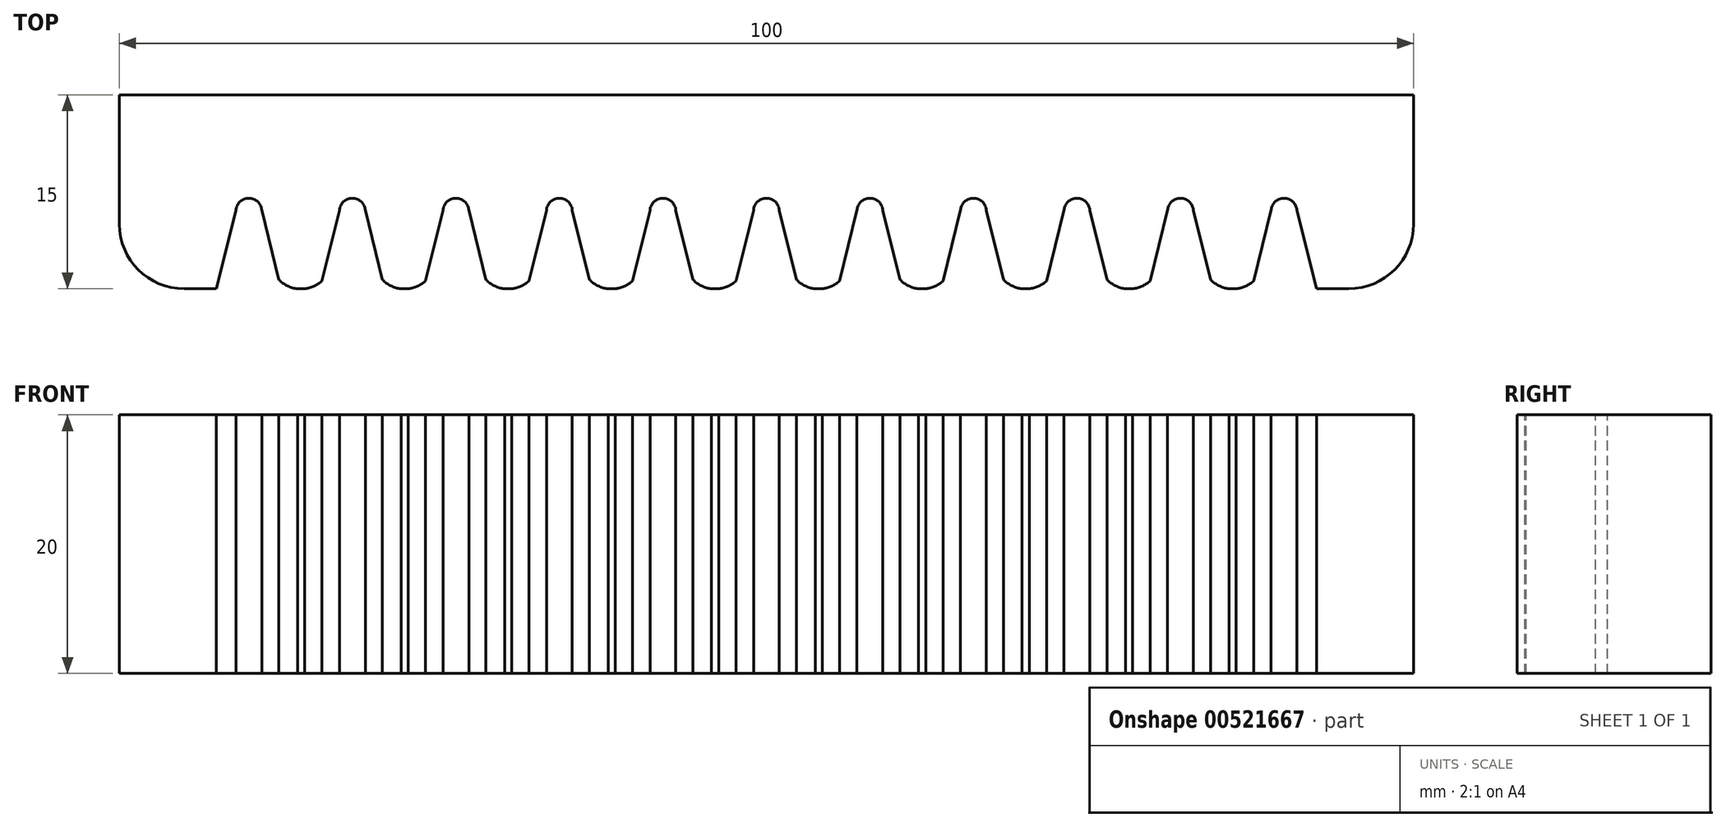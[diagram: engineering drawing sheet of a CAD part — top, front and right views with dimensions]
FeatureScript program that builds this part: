
annotation { "Feature Type Name" : "Feature", "Feature Type Description" : "" }
export const myFeature = defineFeature(function(context is Context, id is Id, definition is map)
    precondition{}
    {
        {
            var Q0;
            Q0=qCreatedBy(makeId("Front.planeOp"),FACE);
            var sketch = newSketch(context, id + "F0", { "sketchPlane" : qUnion([Q0])});
            skLineSegment(sketch, "E0.bottom", {"start": v(50, -10) * mm, "end": v(-50, -10) * mm});
            skLineSegment(sketch, "E0.top", {"start": v(50, 10) * mm, "end": v(-50, 10) * mm});
            skLineSegment(sketch, "E0.left", {"start": v(50, -10) * mm, "end": v(50, 10) * mm});
            skLineSegment(sketch, "E0.right", {"start": v(-50, -10) * mm, "end": v(-50, 10) * mm});
            skPoint(sketch, "E0.middle", {"position": v(0, 0) * mm});
            skSolve(sketch);
        }
        {
            var Q0;
            Q0 = qSketchRegion(id + "F0", true);
            extrude(context, id + "F1", {"entities" : qUnion([Q0]), "depth" : 15 * mm, "offsetDistance" : 25 * mm});
        }
        {
            var Q0;
            Q0=makeQuery(id+"F1.opExtrude","SWEPT_FACE",FACE,{"disambiguationData":[OSD([sQuery(id+"F0.wireOp",EDGE,"E0.top")])]});
            var sketch = newSketch(context, id + "F2", { "sketchPlane" : qUnion([Q0])});
            skLineSegment(sketch, "E1", {"start": v(0, 0) * mm, "end": v(0, -15) * mm, "construction": true});
            skArc(sketch, "E2", {"start": v(1, -8.94) * mm, "mid": v(0, -8) * mm, "end": v(-1, -8.94) * mm});
            skLineSegment(sketch, "E3", {"start": v(-1, -8.94) * mm, "end": v(-2.5, -15) * mm});
            skLineSegment(sketch, "E4.MirrorCS", {"start": v(1, -8.94) * mm, "end": v(2.5, -15) * mm});
            skPoint(sketch, "E5.center.orphan", {"position": v(0, -12.5) * mm});
            skPoint(sketch, "E6.center.orphan", {"position": v(0, -10.5) * mm});
            skLineSegment(sketch, "E7.1.0.0", {"start": v(9, -8.94) * mm, "end": v(10.5, -15) * mm});
            skArc(sketch, "E7.1.0.1", {"start": v(9, -8.94) * mm, "mid": v(8, -8) * mm, "end": v(7, -8.94) * mm});
            skLineSegment(sketch, "E7.1.0.2", {"start": v(7, -8.94) * mm, "end": v(5.5, -15) * mm});
            skLineSegment(sketch, "E7.2.0.0", {"start": v(17, -8.94) * mm, "end": v(18.5, -15) * mm});
            skArc(sketch, "E7.2.0.1", {"start": v(17, -8.94) * mm, "mid": v(16, -8) * mm, "end": v(15, -8.94) * mm});
            skLineSegment(sketch, "E7.2.0.2", {"start": v(15, -8.94) * mm, "end": v(13.5, -15) * mm});
            skLineSegment(sketch, "E7.3.0.0", {"start": v(25, -8.94) * mm, "end": v(26.5, -15) * mm});
            skArc(sketch, "E7.3.0.1", {"start": v(25, -8.94) * mm, "mid": v(24, -8) * mm, "end": v(23, -8.94) * mm});
            skLineSegment(sketch, "E7.3.0.2", {"start": v(23, -8.94) * mm, "end": v(21.5, -15) * mm});
            skLineSegment(sketch, "E7.4.0.0", {"start": v(33, -8.94) * mm, "end": v(34.5, -15) * mm});
            skArc(sketch, "E7.4.0.1", {"start": v(33, -8.94) * mm, "mid": v(32, -8) * mm, "end": v(31, -8.94) * mm});
            skLineSegment(sketch, "E7.4.0.2", {"start": v(31, -8.94) * mm, "end": v(29.5, -15) * mm});
            skLineSegment(sketch, "E7.5.0.0", {"start": v(41, -8.94) * mm, "end": v(42.5, -15) * mm});
            skArc(sketch, "E7.5.0.1", {"start": v(41, -8.94) * mm, "mid": v(40, -8) * mm, "end": v(39, -8.94) * mm});
            skLineSegment(sketch, "E7.5.0.2", {"start": v(39, -8.94) * mm, "end": v(37.5, -15) * mm});
            skLineSegment(sketch, "E7.direction1", {"start": v(2.5, -15) * mm, "end": v(10.5, -15) * mm, "construction": true});
            skLineSegment(sketch, "E8.1.0.0", {"start": v(-9, -8.94) * mm, "end": v(-10.5, -15) * mm});
            skArc(sketch, "E8.1.0.1", {"start": v(-7, -8.94) * mm, "mid": v(-8, -8) * mm, "end": v(-9, -8.94) * mm});
            skLineSegment(sketch, "E8.1.0.2", {"start": v(-7, -8.94) * mm, "end": v(-5.5, -15) * mm});
            skLineSegment(sketch, "E8.2.0.0", {"start": v(-17, -8.94) * mm, "end": v(-18.5, -15) * mm});
            skArc(sketch, "E8.2.0.1", {"start": v(-15, -8.94) * mm, "mid": v(-16, -8) * mm, "end": v(-17, -8.94) * mm});
            skLineSegment(sketch, "E8.2.0.2", {"start": v(-15, -8.94) * mm, "end": v(-13.5, -15) * mm});
            skLineSegment(sketch, "E8.3.0.0", {"start": v(-25, -8.94) * mm, "end": v(-26.5, -15) * mm});
            skArc(sketch, "E8.3.0.1", {"start": v(-23, -8.94) * mm, "mid": v(-24, -8) * mm, "end": v(-25, -8.94) * mm});
            skLineSegment(sketch, "E8.3.0.2", {"start": v(-23, -8.94) * mm, "end": v(-21.5, -15) * mm});
            skLineSegment(sketch, "E8.4.0.0", {"start": v(-33, -8.94) * mm, "end": v(-34.5, -15) * mm});
            skArc(sketch, "E8.4.0.1", {"start": v(-31, -8.94) * mm, "mid": v(-32, -8) * mm, "end": v(-33, -8.94) * mm});
            skLineSegment(sketch, "E8.4.0.2", {"start": v(-31, -8.94) * mm, "end": v(-29.5, -15) * mm});
            skLineSegment(sketch, "E8.5.0.0", {"start": v(-41, -8.94) * mm, "end": v(-42.5, -15) * mm});
            skArc(sketch, "E8.5.0.1", {"start": v(-39, -8.94) * mm, "mid": v(-40, -8) * mm, "end": v(-41, -8.94) * mm});
            skLineSegment(sketch, "E8.5.0.2", {"start": v(-39, -8.94) * mm, "end": v(-37.5, -15) * mm});
            skLineSegment(sketch, "E8.direction1", {"start": v(-2.5, -15) * mm, "end": v(-10.5, -15) * mm, "construction": true});
            skArc(sketch, "E9", {"start": v(2.33, -14.3) * mm, "mid": v(3.97, -15.01) * mm, "end": v(5.65, -14.39) * mm});
            skArc(sketch, "E10.1.0.0", {"start": v(10.33, -14.3) * mm, "mid": v(11.97, -15.01) * mm, "end": v(13.65, -14.39) * mm});
            skArc(sketch, "E10.2.0.0", {"start": v(18.33, -14.3) * mm, "mid": v(19.97, -15.01) * mm, "end": v(21.65, -14.39) * mm});
            skArc(sketch, "E10.3.0.0", {"start": v(26.33, -14.3) * mm, "mid": v(27.97, -15.01) * mm, "end": v(29.65, -14.39) * mm});
            skArc(sketch, "E10.4.0.0", {"start": v(34.33, -14.3) * mm, "mid": v(35.97, -15.01) * mm, "end": v(37.65, -14.39) * mm});
            skLineSegment(sketch, "E10.direction1", {"start": v(2.33, -14.3) * mm, "end": v(10.33, -14.3) * mm, "construction": true});
            skArc(sketch, "E11.1.0.0", {"start": v(-5.67, -14.3) * mm, "mid": v(-4.03, -15.01) * mm, "end": v(-2.35, -14.39) * mm});
            skArc(sketch, "E11.2.0.0", {"start": v(-13.67, -14.3) * mm, "mid": v(-12.03, -15.01) * mm, "end": v(-10.35, -14.39) * mm});
            skArc(sketch, "E11.3.0.0", {"start": v(-21.67, -14.3) * mm, "mid": v(-20.03, -15.01) * mm, "end": v(-18.35, -14.39) * mm});
            skArc(sketch, "E11.4.0.0", {"start": v(-29.67, -14.3) * mm, "mid": v(-28.03, -15.01) * mm, "end": v(-26.35, -14.39) * mm});
            skArc(sketch, "E11.5.0.0", {"start": v(-37.67, -14.3) * mm, "mid": v(-36.03, -15.01) * mm, "end": v(-34.35, -14.39) * mm});
            skLineSegment(sketch, "E11.direction1", {"start": v(2.33, -14.3) * mm, "end": v(-5.67, -14.3) * mm, "construction": true});
            skSolve(sketch);
        }
        {
            var Q0;
            {var subQ0=sQuery(id+"F2.wireOp",EDGE,"E8.5.0.0");Q0=makeQuery(id+"F2.imprint","IMPRINT",FACE,{"disambiguationData":[TD([[makeQuery(id+"F2.imprint","IMPRINT",EDGE,{"derivedFrom":subQ0}),1.0]])]});}
            var Q1;
            {var subQ0=sQuery(id+"F2.wireOp",EDGE,"E8.4.0.0");Q1=makeQuery(id+"F2.imprint","IMPRINT",FACE,{"disambiguationData":[TD([[makeQuery(id+"F2.imprint","IMPRINT",EDGE,{"derivedFrom":subQ0}),1.0]])]});}
            var Q2;
            {var subQ0=sQuery(id+"F2.wireOp",EDGE,"E8.3.0.0");Q2=makeQuery(id+"F2.imprint","IMPRINT",FACE,{"disambiguationData":[TD([[makeQuery(id+"F2.imprint","IMPRINT",EDGE,{"derivedFrom":subQ0}),1.0]])]});}
            var Q3;
            {var subQ0=sQuery(id+"F2.wireOp",EDGE,"E8.2.0.0");Q3=makeQuery(id+"F2.imprint","IMPRINT",FACE,{"disambiguationData":[TD([[makeQuery(id+"F2.imprint","IMPRINT",EDGE,{"derivedFrom":subQ0}),1.0]])]});}
            var Q4;
            {var subQ0=sQuery(id+"F2.wireOp",EDGE,"E8.1.0.0");Q4=makeQuery(id+"F2.imprint","IMPRINT",FACE,{"disambiguationData":[TD([[makeQuery(id+"F2.imprint","IMPRINT",EDGE,{"derivedFrom":subQ0}),1.0]])]});}
            var Q5;
            Q5=makeQuery(id+"F2.imprint","IMPRINT",FACE,{"disambiguationData":[TD([[makeQuery(id+"F2.imprint","IMPRINT",EDGE,{"derivedFrom":sQuery(id+"F2.wireOp",EDGE,"E2")}),1.0]])]});
            var Q6;
            {var subQ0=sQuery(id+"F2.wireOp",EDGE,"E7.1.0.0");Q6=makeQuery(id+"F2.imprint","IMPRINT",FACE,{"disambiguationData":[TD([[makeQuery(id+"F2.imprint","IMPRINT",EDGE,{"derivedFrom":subQ0}),-1.0]])]});}
            var Q7;
            {var subQ0=sQuery(id+"F2.wireOp",EDGE,"E7.2.0.0");Q7=makeQuery(id+"F2.imprint","IMPRINT",FACE,{"disambiguationData":[TD([[makeQuery(id+"F2.imprint","IMPRINT",EDGE,{"derivedFrom":subQ0}),-1.0]])]});}
            var Q8;
            {var subQ0=sQuery(id+"F2.wireOp",EDGE,"E7.3.0.0");Q8=makeQuery(id+"F2.imprint","IMPRINT",FACE,{"disambiguationData":[TD([[makeQuery(id+"F2.imprint","IMPRINT",EDGE,{"derivedFrom":subQ0}),-1.0]])]});}
            var Q9;
            {var subQ0=sQuery(id+"F2.wireOp",EDGE,"E7.4.0.0");Q9=makeQuery(id+"F2.imprint","IMPRINT",FACE,{"disambiguationData":[TD([[makeQuery(id+"F2.imprint","IMPRINT",EDGE,{"derivedFrom":subQ0}),-1.0]])]});}
            var Q10;
            {var subQ0=sQuery(id+"F2.wireOp",EDGE,"E7.5.0.0");Q10=makeQuery(id+"F2.imprint","IMPRINT",FACE,{"disambiguationData":[TD([[makeQuery(id+"F2.imprint","IMPRINT",EDGE,{"derivedFrom":subQ0}),-1.0]])]});}
            var Q11;
            {var subQ0=sQuery(id+"F2.wireOp",EDGE,"E7.2.0.2");var subQ1=makeQuery(id+"F1.opExtrude","CAP_EDGE",EDGE,{"disambiguationData":[OSD([sQuery(id+"F0.wireOp",EDGE,"E0.top")])],"isStart":false});var subQ2=makeQuery(id+"F2.imprint","INTERSECT",VERTEX,{"derivedFrom":[subQ1,subQ0]});Q11=makeQuery(id+"F2.imprint","IMPRINT",FACE,{"disambiguationData":[TD([[makeQuery(id+"F2.imprint","IMPRINT",EDGE,{"disambiguationData":[TD([[subQ2,1.0]])],"derivedFrom":subQ0}),-1.0]])]});}
            var Q12;
            {var subQ0=sQuery(id+"F2.wireOp",EDGE,"E7.1.0.0");var subQ1=makeQuery(id+"F1.opExtrude","CAP_EDGE",EDGE,{"disambiguationData":[OSD([sQuery(id+"F0.wireOp",EDGE,"E0.top")])],"isStart":false});var subQ2=makeQuery(id+"F2.imprint","INTERSECT",VERTEX,{"derivedFrom":[subQ1,subQ0]});Q12=makeQuery(id+"F2.imprint","IMPRINT",FACE,{"disambiguationData":[TD([[makeQuery(id+"F2.imprint","IMPRINT",EDGE,{"disambiguationData":[TD([[subQ2,1.0]])],"derivedFrom":subQ0}),1.0]])]});}
            var Q13;
            {var subQ0=sQuery(id+"F2.wireOp",EDGE,"E7.2.0.0");var subQ1=makeQuery(id+"F1.opExtrude","CAP_EDGE",EDGE,{"disambiguationData":[OSD([sQuery(id+"F0.wireOp",EDGE,"E0.top")])],"isStart":false});var subQ2=makeQuery(id+"F2.imprint","INTERSECT",VERTEX,{"derivedFrom":[subQ1,subQ0]});Q13=makeQuery(id+"F2.imprint","IMPRINT",FACE,{"disambiguationData":[TD([[makeQuery(id+"F2.imprint","IMPRINT",EDGE,{"disambiguationData":[TD([[subQ2,1.0]])],"derivedFrom":subQ0}),1.0]])]});}
            var Q14;
            {var subQ0=sQuery(id+"F2.wireOp",EDGE,"E7.3.0.2");var subQ1=makeQuery(id+"F1.opExtrude","CAP_EDGE",EDGE,{"disambiguationData":[OSD([sQuery(id+"F0.wireOp",EDGE,"E0.top")])],"isStart":false});var subQ2=makeQuery(id+"F2.imprint","INTERSECT",VERTEX,{"derivedFrom":[subQ1,subQ0]});Q14=makeQuery(id+"F2.imprint","IMPRINT",FACE,{"disambiguationData":[TD([[makeQuery(id+"F2.imprint","IMPRINT",EDGE,{"disambiguationData":[TD([[subQ2,1.0]])],"derivedFrom":subQ0}),-1.0]])]});}
            var Q15;
            {var subQ0=sQuery(id+"F2.wireOp",EDGE,"E7.3.0.0");var subQ1=makeQuery(id+"F1.opExtrude","CAP_EDGE",EDGE,{"disambiguationData":[OSD([sQuery(id+"F0.wireOp",EDGE,"E0.top")])],"isStart":false});var subQ2=makeQuery(id+"F2.imprint","INTERSECT",VERTEX,{"derivedFrom":[subQ1,subQ0]});Q15=makeQuery(id+"F2.imprint","IMPRINT",FACE,{"disambiguationData":[TD([[makeQuery(id+"F2.imprint","IMPRINT",EDGE,{"disambiguationData":[TD([[subQ2,1.0]])],"derivedFrom":subQ0}),1.0]])]});}
            var Q16;
            {var subQ0=sQuery(id+"F2.wireOp",EDGE,"E7.4.0.2");var subQ1=makeQuery(id+"F1.opExtrude","CAP_EDGE",EDGE,{"disambiguationData":[OSD([sQuery(id+"F0.wireOp",EDGE,"E0.top")])],"isStart":false});var subQ2=makeQuery(id+"F2.imprint","INTERSECT",VERTEX,{"derivedFrom":[subQ1,subQ0]});Q16=makeQuery(id+"F2.imprint","IMPRINT",FACE,{"disambiguationData":[TD([[makeQuery(id+"F2.imprint","IMPRINT",EDGE,{"disambiguationData":[TD([[subQ2,1.0]])],"derivedFrom":subQ0}),-1.0]])]});}
            var Q17;
            {var subQ0=sQuery(id+"F2.wireOp",EDGE,"E7.4.0.0");var subQ1=makeQuery(id+"F1.opExtrude","CAP_EDGE",EDGE,{"disambiguationData":[OSD([sQuery(id+"F0.wireOp",EDGE,"E0.top")])],"isStart":false});var subQ2=makeQuery(id+"F2.imprint","INTERSECT",VERTEX,{"derivedFrom":[subQ1,subQ0]});Q17=makeQuery(id+"F2.imprint","IMPRINT",FACE,{"disambiguationData":[TD([[makeQuery(id+"F2.imprint","IMPRINT",EDGE,{"disambiguationData":[TD([[subQ2,1.0]])],"derivedFrom":subQ0}),1.0]])]});}
            var Q18;
            {var subQ0=sQuery(id+"F2.wireOp",EDGE,"E7.5.0.2");var subQ1=makeQuery(id+"F1.opExtrude","CAP_EDGE",EDGE,{"disambiguationData":[OSD([sQuery(id+"F0.wireOp",EDGE,"E0.top")])],"isStart":false});var subQ2=makeQuery(id+"F2.imprint","INTERSECT",VERTEX,{"derivedFrom":[subQ1,subQ0]});Q18=makeQuery(id+"F2.imprint","IMPRINT",FACE,{"disambiguationData":[TD([[makeQuery(id+"F2.imprint","IMPRINT",EDGE,{"disambiguationData":[TD([[subQ2,1.0]])],"derivedFrom":subQ0}),-1.0]])]});}
            var Q19;
            {var subQ0=sQuery(id+"F2.wireOp",EDGE,"E7.1.0.2");var subQ1=makeQuery(id+"F1.opExtrude","CAP_EDGE",EDGE,{"disambiguationData":[OSD([sQuery(id+"F0.wireOp",EDGE,"E0.top")])],"isStart":false});var subQ2=makeQuery(id+"F2.imprint","INTERSECT",VERTEX,{"derivedFrom":[subQ1,subQ0]});Q19=makeQuery(id+"F2.imprint","IMPRINT",FACE,{"disambiguationData":[TD([[makeQuery(id+"F2.imprint","IMPRINT",EDGE,{"disambiguationData":[TD([[subQ2,1.0]])],"derivedFrom":subQ0}),-1.0]])]});}
            var Q20;
            {var subQ0=sQuery(id+"F2.wireOp",EDGE,"E4.MirrorCS");var subQ1=makeQuery(id+"F1.opExtrude","CAP_EDGE",EDGE,{"disambiguationData":[OSD([sQuery(id+"F0.wireOp",EDGE,"E0.top")])],"isStart":false});var subQ2=makeQuery(id+"F2.imprint","INTERSECT",VERTEX,{"derivedFrom":[subQ1,subQ0]});Q20=makeQuery(id+"F2.imprint","IMPRINT",FACE,{"disambiguationData":[TD([[makeQuery(id+"F2.imprint","IMPRINT",EDGE,{"disambiguationData":[TD([[subQ2,1.0]])],"derivedFrom":subQ0}),1.0]])]});}
            var Q21;
            {var subQ0=sQuery(id+"F2.wireOp",EDGE,"E3");var subQ1=makeQuery(id+"F1.opExtrude","CAP_EDGE",EDGE,{"disambiguationData":[OSD([sQuery(id+"F0.wireOp",EDGE,"E0.top")])],"isStart":false});var subQ2=makeQuery(id+"F2.imprint","INTERSECT",VERTEX,{"derivedFrom":[subQ1,subQ0]});Q21=makeQuery(id+"F2.imprint","IMPRINT",FACE,{"disambiguationData":[TD([[makeQuery(id+"F2.imprint","IMPRINT",EDGE,{"disambiguationData":[TD([[subQ2,1.0]])],"derivedFrom":subQ0}),-1.0]])]});}
            var Q22;
            {var subQ0=sQuery(id+"F2.wireOp",EDGE,"E8.1.0.2");var subQ1=makeQuery(id+"F1.opExtrude","CAP_EDGE",EDGE,{"disambiguationData":[OSD([sQuery(id+"F0.wireOp",EDGE,"E0.top")])],"isStart":false});var subQ2=makeQuery(id+"F2.imprint","INTERSECT",VERTEX,{"derivedFrom":[subQ1,subQ0]});Q22=makeQuery(id+"F2.imprint","IMPRINT",FACE,{"disambiguationData":[TD([[makeQuery(id+"F2.imprint","IMPRINT",EDGE,{"disambiguationData":[TD([[subQ2,1.0]])],"derivedFrom":subQ0}),1.0]])]});}
            var Q23;
            {var subQ0=sQuery(id+"F2.wireOp",EDGE,"E8.1.0.0");var subQ1=makeQuery(id+"F1.opExtrude","CAP_EDGE",EDGE,{"disambiguationData":[OSD([sQuery(id+"F0.wireOp",EDGE,"E0.top")])],"isStart":false});var subQ2=makeQuery(id+"F2.imprint","INTERSECT",VERTEX,{"derivedFrom":[subQ1,subQ0]});Q23=makeQuery(id+"F2.imprint","IMPRINT",FACE,{"disambiguationData":[TD([[makeQuery(id+"F2.imprint","IMPRINT",EDGE,{"disambiguationData":[TD([[subQ2,1.0]])],"derivedFrom":subQ0}),-1.0]])]});}
            var Q24;
            {var subQ0=sQuery(id+"F2.wireOp",EDGE,"E8.2.0.2");var subQ1=makeQuery(id+"F1.opExtrude","CAP_EDGE",EDGE,{"disambiguationData":[OSD([sQuery(id+"F0.wireOp",EDGE,"E0.top")])],"isStart":false});var subQ2=makeQuery(id+"F2.imprint","INTERSECT",VERTEX,{"derivedFrom":[subQ1,subQ0]});Q24=makeQuery(id+"F2.imprint","IMPRINT",FACE,{"disambiguationData":[TD([[makeQuery(id+"F2.imprint","IMPRINT",EDGE,{"disambiguationData":[TD([[subQ2,1.0]])],"derivedFrom":subQ0}),1.0]])]});}
            var Q25;
            {var subQ0=sQuery(id+"F2.wireOp",EDGE,"E8.2.0.0");var subQ1=makeQuery(id+"F1.opExtrude","CAP_EDGE",EDGE,{"disambiguationData":[OSD([sQuery(id+"F0.wireOp",EDGE,"E0.top")])],"isStart":false});var subQ2=makeQuery(id+"F2.imprint","INTERSECT",VERTEX,{"derivedFrom":[subQ1,subQ0]});Q25=makeQuery(id+"F2.imprint","IMPRINT",FACE,{"disambiguationData":[TD([[makeQuery(id+"F2.imprint","IMPRINT",EDGE,{"disambiguationData":[TD([[subQ2,1.0]])],"derivedFrom":subQ0}),-1.0]])]});}
            var Q26;
            {var subQ0=sQuery(id+"F2.wireOp",EDGE,"E8.3.0.2");var subQ1=makeQuery(id+"F1.opExtrude","CAP_EDGE",EDGE,{"disambiguationData":[OSD([sQuery(id+"F0.wireOp",EDGE,"E0.top")])],"isStart":false});var subQ2=makeQuery(id+"F2.imprint","INTERSECT",VERTEX,{"derivedFrom":[subQ1,subQ0]});Q26=makeQuery(id+"F2.imprint","IMPRINT",FACE,{"disambiguationData":[TD([[makeQuery(id+"F2.imprint","IMPRINT",EDGE,{"disambiguationData":[TD([[subQ2,1.0]])],"derivedFrom":subQ0}),1.0]])]});}
            var Q27;
            {var subQ0=sQuery(id+"F2.wireOp",EDGE,"E8.3.0.0");var subQ1=makeQuery(id+"F1.opExtrude","CAP_EDGE",EDGE,{"disambiguationData":[OSD([sQuery(id+"F0.wireOp",EDGE,"E0.top")])],"isStart":false});var subQ2=makeQuery(id+"F2.imprint","INTERSECT",VERTEX,{"derivedFrom":[subQ1,subQ0]});Q27=makeQuery(id+"F2.imprint","IMPRINT",FACE,{"disambiguationData":[TD([[makeQuery(id+"F2.imprint","IMPRINT",EDGE,{"disambiguationData":[TD([[subQ2,1.0]])],"derivedFrom":subQ0}),-1.0]])]});}
            var Q28;
            {var subQ0=sQuery(id+"F2.wireOp",EDGE,"E8.4.0.2");var subQ1=makeQuery(id+"F1.opExtrude","CAP_EDGE",EDGE,{"disambiguationData":[OSD([sQuery(id+"F0.wireOp",EDGE,"E0.top")])],"isStart":false});var subQ2=makeQuery(id+"F2.imprint","INTERSECT",VERTEX,{"derivedFrom":[subQ1,subQ0]});Q28=makeQuery(id+"F2.imprint","IMPRINT",FACE,{"disambiguationData":[TD([[makeQuery(id+"F2.imprint","IMPRINT",EDGE,{"disambiguationData":[TD([[subQ2,1.0]])],"derivedFrom":subQ0}),1.0]])]});}
            var Q29;
            {var subQ0=sQuery(id+"F2.wireOp",EDGE,"E8.4.0.0");var subQ1=makeQuery(id+"F1.opExtrude","CAP_EDGE",EDGE,{"disambiguationData":[OSD([sQuery(id+"F0.wireOp",EDGE,"E0.top")])],"isStart":false});var subQ2=makeQuery(id+"F2.imprint","INTERSECT",VERTEX,{"derivedFrom":[subQ1,subQ0]});Q29=makeQuery(id+"F2.imprint","IMPRINT",FACE,{"disambiguationData":[TD([[makeQuery(id+"F2.imprint","IMPRINT",EDGE,{"disambiguationData":[TD([[subQ2,1.0]])],"derivedFrom":subQ0}),-1.0]])]});}
            var Q30;
            {var subQ0=sQuery(id+"F2.wireOp",EDGE,"E8.5.0.2");var subQ1=makeQuery(id+"F1.opExtrude","CAP_EDGE",EDGE,{"disambiguationData":[OSD([sQuery(id+"F0.wireOp",EDGE,"E0.top")])],"isStart":false});var subQ2=makeQuery(id+"F2.imprint","INTERSECT",VERTEX,{"derivedFrom":[subQ1,subQ0]});Q30=makeQuery(id+"F2.imprint","IMPRINT",FACE,{"disambiguationData":[TD([[makeQuery(id+"F2.imprint","IMPRINT",EDGE,{"disambiguationData":[TD([[subQ2,1.0]])],"derivedFrom":subQ0}),1.0]])]});}
            extrude(context, id + "F3", {"entities" : qUnion([Q0, Q1, Q2, Q3, Q4, Q5, Q6, Q7, Q8, Q9, Q10, Q11, Q12, Q13, Q14, Q15, Q16, Q17, Q18, Q19, Q20, Q21, Q22, Q23, Q24, Q25, Q26, Q27, Q28, Q29, Q30]), "operationType" : NewBodyOperationType.REMOVE, "endBound" : BoundingType.UP_TO_NEXT, "oppositeDirection" : true, "depth" : 25 * mm, "offsetDistance" : 25 * mm});
        }
        {
            var Q0;
            Q0=makeQuery(id+"F1.opExtrude","CAP_EDGE",EDGE,{"disambiguationData":[OSD([sQuery(id+"F0.wireOp",EDGE,"E0.right")])],"isStart":false});
            var Q1;
            Q1=makeQuery(id+"F1.opExtrude","CAP_EDGE",EDGE,{"disambiguationData":[OSD([sQuery(id+"F0.wireOp",EDGE,"E0.left")])],"isStart":false});
            fillet(context, id + "F4", {"entities" : qUnion([Q0, Q1]), "radius" : 5 * mm, "tangentPropagation" : true, "allowEdgeOverflow" : false});
        }
    });
